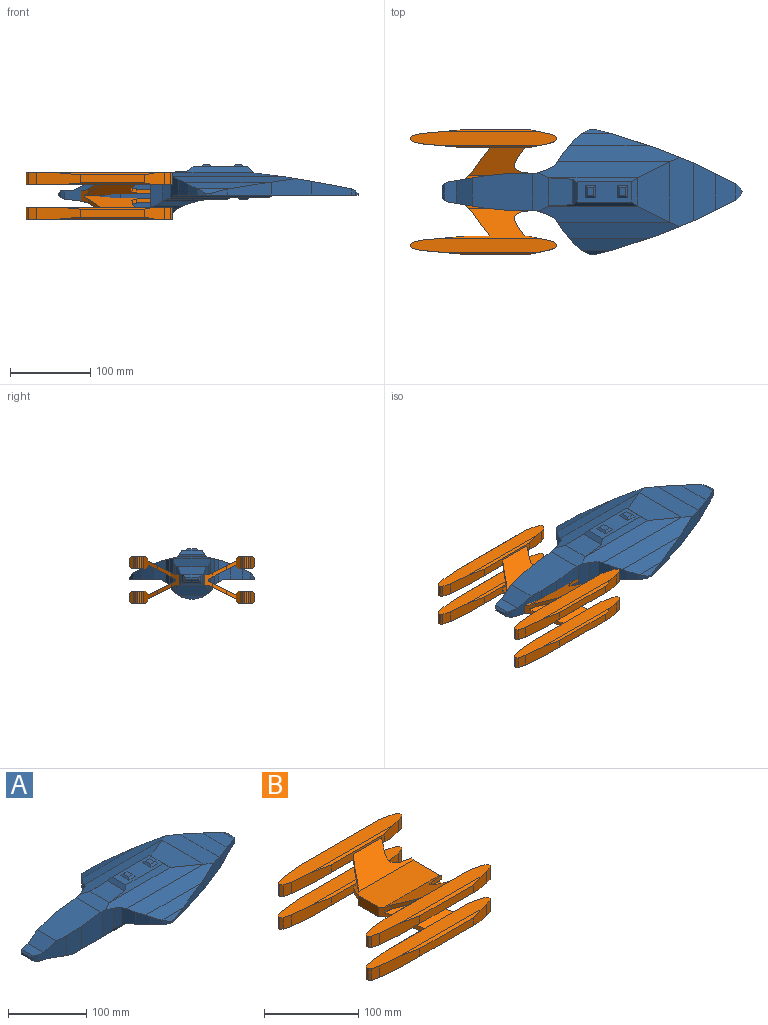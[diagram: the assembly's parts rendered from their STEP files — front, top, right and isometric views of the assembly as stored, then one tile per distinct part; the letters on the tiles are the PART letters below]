
ASSEMBLY  parts=2 mates=3
PART A: 108 faces, bbox 372.5x155x62.5 mm
  f0: plane 7.5x2.5mm, normal (0,-1,0), area 18.8mm2, adj f15,f16,f67,f89
  f1: plane 7.5x2.5mm, normal (0,1,0), area 18.8mm2, adj f27,f28,f67,f84
  f2: plane 10x7.5mm, normal (0,0,1), area 75mm2, adj f53,f68,f78,f91
  f3: plane 10x7.5mm, normal (0,0,1), area 75mm2, adj f69,f77,f79,f90
  f4: plane 67.5x25mm, normal (0,0,1), area 1312.5mm2, adj f52,f53,f68,f69,f75,f77,f78,f79
  f5: plane 7.5x2.5mm, normal (-0.71,-0.71,0), area 17.7mm2, adj f6,f40,f41,f42
  f6: plane 10x5mm, normal (-0.45,-0.89,0), area 48.9mm2, adj f5,f7,f43,f44
  f7: plane 45x31.08mm, normal (-0.16,-0.99,0), area 896.9mm2, adj f6,f8,f44,f45,f46,f47,f48
  f8: plane 36.89x25mm, normal (-0.1,-1,0), area 861.1mm2, adj f7,f9,f46,f47,f103
  f9: plane 40.31x37.5mm, normal (0,-1,0), area 1418.7mm2, adj f8,f10,f47,f50,f103
  f10: plane 40.88x15mm, normal (-0.32,-0.95,0), area 590.7mm2, adj f9,f11,f50,f85,f103,f104
  f11: plane 32.5x10mm, normal (-0.45,-0.89,0), area 331.9mm2, adj f10,f12,f85,f100,f105
  f12: plane 27.5x15mm, normal (-0.83,-0.55,0), area 400mm2, adj f11,f13,f67,f85,f87,f100,f107
  f13: plane 18.75x15mm, normal (-0.77,-0.64,0), area 309.2mm2, adj f12,f14,f67,f87,f88
  f14: plane 12.5x10mm, normal (-0.71,-0.71,0), area 141.4mm2, adj f13,f15,f67,f88
  f15: plane 10x7.5mm, normal (-0.45,-0.89,0), area 55.9mm2, adj f0,f14,f67,f89
  f16: plane 20x7.5mm, normal (0.24,-0.97,0), area 103.1mm2, adj f0,f17,f67,f89
  f17: plane 55x17.5mm, normal (0.3,-0.95,0), area 684.1mm2, adj f16,f18,f67,f87,f88
  f18: plane 50x20.43mm, normal (0.37,-0.93,0), area 991.5mm2, adj f17,f19,f67,f73,f74,f87
  f19: plane 50x25mm, normal (0.45,-0.89,0), area 692.4mm2, adj f18,f20,f67,f72,f74
  f20: plane 7.5x5mm, normal (0.71,-0.71,0), area 44.2mm2, adj f19,f21,f67,f71
  f21: plane 5x5mm, normal (0.89,-0.45,0), area 21mm2, adj f20,f22,f67,f70
  f22: plane 5x5mm, normal (0.89,0.45,0), area 21mm2, adj f21,f23,f67,f70
  f23: plane 7.5x5mm, normal (0.71,0.71,0), area 44.2mm2, adj f22,f24,f67,f71
  f24: plane 50x25mm, normal (0.45,0.89,0), area 692.4mm2, adj f23,f25,f67,f72,f74
  f25: plane 50x20.43mm, normal (0.37,0.93,0), area 991.5mm2, adj f24,f26,f67,f73,f74,f82
  f26: plane 55x17.5mm, normal (0.3,0.95,0), area 684.1mm2, adj f25,f27,f67,f82,f83
  f27: plane 20x7.5mm, normal (0.24,0.97,0), area 103.1mm2, adj f1,f26,f67,f84
  f28: plane 10x7.5mm, normal (-0.45,0.89,0), area 55.9mm2, adj f1,f29,f67,f84
  f29: plane 12.5x10mm, normal (-0.71,0.71,0), area 141.4mm2, adj f28,f30,f67,f83
  f30: plane 18.75x15mm, normal (-0.77,0.64,0), area 309.2mm2, adj f29,f31,f67,f82,f83
  f31: plane 27.5x15mm, normal (-0.83,0.55,0), area 400mm2, adj f30,f32,f67,f80,f82,f92,f94
  f32: plane 32.5x10mm, normal (-0.45,0.89,0), area 331.9mm2, adj f31,f33,f80,f94,f95
  f33: plane 40.88x15mm, normal (-0.32,0.95,0), area 590.7mm2, adj f32,f34,f50,f80,f96,f97
  f34: plane 40.31x37.5mm, normal (0,1,0), area 1418.7mm2, adj f33,f35,f47,f50,f97
  f35: plane 36.89x25mm, normal (-0.1,1,0), area 861.1mm2, adj f34,f36,f46,f47,f97
  f36: plane 45x31.08mm, normal (-0.16,0.99,0), area 896.9mm2, adj f35,f37,f44,f45,f46,f47,f48
  f37: plane 10x5mm, normal (-0.45,0.89,0), area 48.9mm2, adj f36,f38,f43,f44
  f38: plane 7.5x2.5mm, normal (-0.71,0.71,0), area 17.7mm2, adj f37,f40,f41,f42
  f39: plane 15x5mm, normal (0,0,-1), area 75mm2, adj f49,f54,f99,f101
  f40: plane 20x2.5mm, normal (-0.71,0,0.71), area 61.9mm2, adj f5,f38,f41,f44
  f41: plane 15x2.5mm, normal (-1,0,0), area 37.5mm2, adj f5,f38,f40,f42
  f42: plane 20x2.5mm, normal (-0.71,0,-0.71), area 61.9mm2, adj f5,f38,f41,f43
  f43: plane 25x5mm, normal (-0.45,0,-0.89), area 125.8mm2, adj f6,f37,f42,f45
  f44: plane 28.33x15mm, normal (0,0,1), area 379.2mm2, adj f6,f7,f36,f37,f40,f48
  f45: plane 31.67x20mm, normal (-0.12,0,-0.99), area 571.1mm2, adj f7,f36,f43,f46
  f46: plane 47.5x41.88mm, normal (-0.25,0,-0.97), area 1832.8mm2, adj f7,f8,f35,f36,f45,f49,f97,f98
  f47: plane 75x45mm, normal (-0.13,0,0.99), area 3228.3mm2, adj f7,f8,f9,f34,f35,f36,f48,f50
  f48: plane 35x20mm, normal (-0.45,0,0.89), area 708.1mm2, adj f7,f36,f44,f47
  f49: plane 42.5x32.5mm, normal (-0.12,0,-0.99), area 936.1mm2, adj f39,f46,f98,f99,f101,f102
  f50: plane 48x20mm, normal (-0.12,0,0.99), area 868mm2, adj f9,f10,f33,f34,f47,f51,f80,f85
  f51: plane 35x30mm, normal (-0.08,0,1), area 1003.5mm2, adj f50,f52,f81,f86
  f52: plane 31.67x5mm, normal (-0.71,0,0.71), area 200.3mm2, adj f4,f51,f81,f86
  f53: plane 15x2.5mm, normal (-0.71,0,0.71), area 44.2mm2, adj f2,f4,f78,f91
  f54: plane 25x10mm, normal (0.24,0,-0.97), area 154.6mm2, adj f39,f55,f99,f101
  f55: plane 40x5mm, normal (0.71,0,-0.71), area 229.8mm2, adj f54,f56,f98,f102
  f56: plane 50x10mm, normal (0.45,0,-0.89), area 503.1mm2, adj f55,f57,f97,f103
  f57: plane 55x15mm, normal (0.32,0,-0.95), area 830.1mm2, adj f56,f58,f96,f104
  f58: plane 60x15mm, normal (0.16,0,-0.99), area 874.4mm2, adj f57,f59,f95,f105
  f59: plane 60x22.5mm, normal (0,0,-1), area 1350mm2, adj f58,f60,f94,f100
  f60: plane 70x5mm, normal (0.45,0,-0.89), area 363.4mm2, adj f59,f61,f94,f100
  f61: plane 70x7.5mm, normal (0,0,-1), area 525mm2, adj f60,f62,f92,f107
  f62: plane 70x2.5mm, normal (-0.71,0,-0.71), area 229.8mm2, adj f61,f63,f93,f106
  f63: plane 60x10mm, normal (0,0,-1), area 600mm2, adj f62,f64,f93,f106
  f64: plane 70x2.5mm, normal (0.71,0,-0.71), area 229.8mm2, adj f63,f65,f93,f106
  f65: plane 70x25mm, normal (0,0,-1), area 1750mm2, adj f64,f66,f92,f107
  f66: plane 75x5mm, normal (0.45,0,-0.89), area 405.3mm2, adj f65,f67,f92,f107
  f67: plane 229.17x155mm, normal (0,0,-1), area 13491.7mm2, adj f0,f1,f12,f13,f14,f15,f16,f17
  f68: plane 15x2.5mm, normal (0.71,0,0.71), area 44.2mm2, adj f2,f4,f78,f91
  f69: plane 15x2.5mm, normal (-0.71,0,0.71), area 44.2mm2, adj f3,f4,f79,f90
  f70: plane 10x2.5mm, normal (0.71,0,0.71), area 17.7mm2, adj f21,f22,f71
  f71: plane 20x5mm, normal (0.45,0,0.89), area 83.9mm2, adj f20,f23,f70,f72
  f72: plane 45x25mm, normal (0.2,0,0.98), area 828.6mm2, adj f19,f24,f71,f74
  f73: plane 86.05x30mm, normal (0.16,0,0.99), area 2422.4mm2, adj f18,f25,f74,f76,f82,f87
  f74: plane 72x27.5mm, normal (0.18,0,0.98), area 1641.5mm2, adj f18,f19,f24,f25,f72,f73
  f75: plane 35x7.5mm, normal (0.71,0,0.71), area 318.2mm2, adj f4,f76,f81,f86
  f76: plane 75x40mm, normal (0.12,0,0.99), area 2217.1mm2, adj f73,f75,f80,f85
  f77: plane 15x2.5mm, normal (0.71,0,0.71), area 44.2mm2, adj f3,f4,f79,f90
  f78: plane 12.5x2.5mm, normal (0,0.71,0.71), area 35.4mm2, adj f2,f4,f53,f68
  f79: plane 12.5x2.5mm, normal (0,0.71,0.71), area 35.4mm2, adj f3,f4,f69,f77
  f80: plane 163x20mm, normal (0,0.24,0.97), area 2691.4mm2, adj f31,f32,f33,f50,f76,f81,f82
  f81: plane 110x7.5mm, normal (0,0.83,0.55), area 717.4mm2, adj f4,f51,f52,f75,f80
  f82: plane 151.6x20mm, normal (0,0.35,0.94), area 2768.4mm2, adj f25,f26,f30,f31,f73,f80,f83
  f83: plane 98.81x15mm, normal (0,0.45,0.89), area 1147.6mm2, adj f26,f29,f30,f82,f84
  f84: plane 37.5x5mm, normal (0,0.71,0.71), area 159.1mm2, adj f1,f27,f28,f83
  f85: plane 163x20mm, normal (0,-0.24,0.97), area 2691.4mm2, adj f10,f11,f12,f50,f76,f86,f87
  f86: plane 110x7.5mm, normal (0,-0.83,0.55), area 717.4mm2, adj f4,f51,f52,f75,f85
  f87: plane 151.6x20mm, normal (0,-0.35,0.94), area 2768.4mm2, adj f12,f13,f17,f18,f73,f85,f88
  f88: plane 98.81x15mm, normal (0,-0.45,0.89), area 1147.6mm2, adj f13,f14,f17,f87,f89
  f89: plane 37.5x5mm, normal (0,-0.71,0.71), area 159.1mm2, adj f0,f15,f16,f88
  f90: plane 12.5x2.5mm, normal (0,-0.71,0.71), area 35.4mm2, adj f3,f4,f69,f77
  f91: plane 12.5x2.5mm, normal (0,-0.71,0.71), area 35.4mm2, adj f2,f4,f53,f68
  f92: plane 125.83x2.5mm, normal (0,0.71,-0.71), area 433.1mm2, adj f31,f61,f65,f66,f67,f93,f94
  f93: plane 15x5mm, normal (0,0.45,-0.89), area 69.9mm2, adj f62,f63,f64,f92
  f94: plane 80x5mm, normal (0,0.45,-0.89), area 409.9mm2, adj f31,f32,f59,f60,f92,f95
  f95: plane 57.5x2.5mm, normal (0,0.71,-0.71), area 167.9mm2, adj f32,f58,f94,f96
  f96: plane 50x5mm, normal (0,0.89,-0.45), area 216.6mm2, adj f33,f57,f95,f97
  f97: plane 95.58x5mm, normal (0,0.71,-0.71), area 420mm2, adj f33,f34,f35,f46,f56,f96,f98
  f98: plane 82x7.5mm, normal (0,0.55,-0.83), area 604.5mm2, adj f46,f49,f55,f97,f99
  f99: plane 46.25x10mm, normal (0,0.24,-0.97), area 315.7mm2, adj f39,f49,f54,f98
  f100: plane 80x5mm, normal (0,-0.45,-0.89), area 409.9mm2, adj f11,f12,f59,f60,f105,f107
  f101: plane 46.25x10mm, normal (0,-0.24,-0.97), area 315.7mm2, adj f39,f49,f54,f102
  f102: plane 82x7.5mm, normal (0,-0.55,-0.83), area 604.5mm2, adj f46,f49,f55,f101,f103
  f103: plane 95.58x5mm, normal (0,-0.71,-0.71), area 420mm2, adj f8,f9,f10,f46,f56,f102,f104
  f104: plane 50x5mm, normal (0,-0.89,-0.45), area 216.6mm2, adj f10,f57,f103,f105
  f105: plane 57.5x2.5mm, normal (0,-0.71,-0.71), area 167.9mm2, adj f11,f58,f100,f104
  f106: plane 15x5mm, normal (0,-0.45,-0.89), area 69.9mm2, adj f62,f63,f64,f107
  f107: plane 125.83x2.5mm, normal (0,-0.71,-0.71), area 433.1mm2, adj f12,f61,f65,f66,f67,f100,f106
PART B: 136 faces, bbox 182.5x155x57.5 mm
  f0: plane 80x10mm, normal (0,1,0), area 587.5mm2, adj f61,f62,f75,f76,f120,f122,f126,f128
  f1: plane 15x2.5mm, normal (-1,0,0), area 37.5mm2, adj f53,f64,f66,f125
  f2: plane 80x10mm, normal (0,1,0), area 587.5mm2, adj f10,f11,f25,f26,f104,f106,f130,f131
  f3: plane 80x10mm, normal (0,-1,0), area 587.5mm2, adj f37,f38,f50,f51,f109,f113,f118,f121
  f4: plane 80x10mm, normal (0,1,0), area 800mm2, adj f44,f45,f111,f124
  f5: plane 80x10mm, normal (0,1,0), area 800mm2, adj f95,f96,f117,f123
  f6: plane 15x2.5mm, normal (-1,0,0), area 37.5mm2, adj f55,f98,f99,f115
  f7: plane 15x2.5mm, normal (-1,0,0), area 37.5mm2, adj f47,f48,f54,f110
  f8: plane 80x10mm, normal (0,-1,0), area 587.5mm2, adj f88,f89,f101,f102,f105,f107,f112,f116
  f9: plane 17.5x13.75mm, normal (-0.81,-0.58,0), area 107.5mm2, adj f10,f59,f106,f130
  f10: plane 12.5x11.25mm, normal (-0.78,-0.62,0), area 80mm2, adj f2,f9,f106,f130
  f11: plane 55x15mm, normal (-0.09,1,0), area 759.4mm2, adj f2,f12,f56,f104,f131,f132
  f12: plane 15x10mm, normal (-0.24,0.97,0), area 154.6mm2, adj f11,f13,f56,f132
  f13: plane 15x2.5mm, normal (-0.71,0.71,0), area 53mm2, adj f12,f56,f65,f132
  f14: plane 15x2.5mm, normal (-0.71,-0.71,0), area 53mm2, adj f15,f56,f65,f132
  f15: plane 15x10mm, normal (-0.24,-0.97,0), area 154.6mm2, adj f14,f16,f56,f132
  f16: plane 55x15mm, normal (-0.09,-1,0), area 759.4mm2, adj f15,f18,f56,f132,f133,f134
  f17: plane 80x10mm, normal (0,-1,0), area 800mm2, adj f68,f69,f127,f135
  f18: plane 80x10mm, normal (0,-1,0), area 800mm2, adj f16,f19,f133,f134
  f19: plane 25x15mm, normal (0.2,-0.98,0), area 350.6mm2, adj f18,f20,f56,f132,f133,f134
  f20: plane 15x7.5mm, normal (0.32,-0.95,0), area 118.6mm2, adj f19,f21,f56,f132
  f21: plane 15x2.5mm, normal (0.71,-0.71,0), area 53mm2, adj f20,f22,f56,f132
  f22: plane 15x2.5mm, normal (1,0,0), area 37.5mm2, adj f21,f23,f56,f132
  f23: plane 15x2.5mm, normal (0.71,0.71,0), area 53mm2, adj f22,f24,f56,f132
  f24: plane 15x7.5mm, normal (0.32,0.95,0), area 118.6mm2, adj f23,f25,f56,f132
  f25: plane 25x15mm, normal (0.2,0.98,0), area 350.6mm2, adj f2,f24,f56,f104,f131,f132
  f26: plane 15x12.5mm, normal (0.83,0.55,0), area 90.1mm2, adj f2,f27,f106,f130
  f27: plane 7.5x5mm, normal (0.89,0.45,0), area 28mm2, adj f26,f28,f106,f130
  f28: plane 7.5x5mm, normal (1,0,0), area 25mm2, adj f27,f29,f106,f130
  f29: plane 6.25x2.5mm, normal (0.71,-0.71,0), area 17.7mm2, adj f28,f30,f106,f130
  f30: plane 6.25x5mm, normal (0.45,-0.89,0), area 28mm2, adj f29,f31,f106,f130
  f31: plane 17.5x6.25mm, normal (0.14,-0.99,0), area 88.4mm2, adj f30,f82,f106,f130
  f32: plane 17.5x6.25mm, normal (0.14,0.99,0), area 88.4mm2, adj f33,f82,f113,f118
  f33: plane 6.25x5mm, normal (0.45,0.89,0), area 28mm2, adj f32,f34,f113,f118
  f34: plane 6.25x2.5mm, normal (0.71,0.71,0), area 17.7mm2, adj f33,f35,f113,f118
  f35: plane 7.5x5mm, normal (1,0,0), area 25mm2, adj f34,f36,f113,f118
  f36: plane 7.5x5mm, normal (0.89,-0.45,0), area 28mm2, adj f35,f37,f113,f118
  f37: plane 15x12.5mm, normal (0.83,-0.55,0), area 90.1mm2, adj f3,f36,f113,f118
  f38: plane 25x15mm, normal (0.2,-0.98,0), area 350.6mm2, adj f3,f39,f54,f109,f110,f121
  f39: plane 15x7.5mm, normal (0.32,-0.95,0), area 118.6mm2, adj f38,f40,f54,f110
  f40: plane 15x2.5mm, normal (0.71,-0.71,0), area 53mm2, adj f39,f41,f54,f110
  f41: plane 15x2.5mm, normal (1,0,0), area 37.5mm2, adj f40,f42,f54,f110
  f42: plane 15x2.5mm, normal (0.71,0.71,0), area 53mm2, adj f41,f43,f54,f110
  f43: plane 15x7.5mm, normal (0.32,0.95,0), area 118.6mm2, adj f42,f44,f54,f110
  f44: plane 25x15mm, normal (0.2,0.98,0), area 350.6mm2, adj f4,f43,f54,f110,f111,f124
  f45: plane 55x15mm, normal (-0.09,1,0), area 759.4mm2, adj f4,f46,f54,f110,f111,f124
  f46: plane 15x10mm, normal (-0.24,0.97,0), area 154.6mm2, adj f45,f47,f54,f110
  f47: plane 15x2.5mm, normal (-0.71,0.71,0), area 53mm2, adj f7,f46,f54,f110
  f48: plane 15x2.5mm, normal (-0.71,-0.71,0), area 53mm2, adj f7,f49,f54,f110
  f49: plane 15x10mm, normal (-0.24,-0.97,0), area 154.6mm2, adj f48,f50,f54,f110
  f50: plane 55x15mm, normal (-0.09,-1,0), area 759.4mm2, adj f3,f49,f54,f109,f110,f121
  f51: plane 12.5x11.25mm, normal (-0.78,0.62,0), area 80mm2, adj f3,f52,f113,f118
  f52: plane 17.5x13.75mm, normal (-0.81,0.58,0), area 107.5mm2, adj f51,f57,f113,f118
  f53: plane 182.5x17.5mm, normal (0,0,1), area 2900mm2, adj f1,f62,f63,f64,f66,f67,f68,f69
  f54: plane 182.5x17.5mm, normal (0,0,1), area 2900mm2, adj f7,f38,f39,f40,f41,f42,f43,f44
  f55: plane 182.5x17.5mm, normal (0,0,-1), area 2900mm2, adj f6,f89,f90,f91,f92,f93,f94,f95
  f56: plane 182.5x17.5mm, normal (0,0,-1), area 2900mm2, adj f11,f12,f13,f14,f15,f16,f19,f20
  f57: plane 17.5x10mm, normal (-0.71,0.71,0), area 159.1mm2, adj f52,f58,f103,f107,f108,f112,f113,f114
  f58: plane 30x12.5mm, normal (-1,0,0), area 375mm2, adj f57,f59,f108,f119
  f59: plane 17.5x10mm, normal (-0.71,-0.71,0), area 159.1mm2, adj f9,f58,f60,f106,f108,f119,f120,f128
  f60: plane 17.5x13.75mm, normal (-0.81,-0.58,0), area 107.5mm2, adj f59,f61,f120,f128
  f61: plane 12.5x11.25mm, normal (-0.78,-0.62,0), area 80mm2, adj f0,f60,f120,f128
  f62: plane 55x15mm, normal (-0.09,1,0), area 759.4mm2, adj f0,f53,f63,f122,f125,f126
  f63: plane 15x10mm, normal (-0.24,0.97,0), area 154.6mm2, adj f53,f62,f64,f125
  f64: plane 15x2.5mm, normal (-0.71,0.71,0), area 53mm2, adj f1,f53,f63,f125
  f65: plane 15x2.5mm, normal (-1,0,0), area 37.5mm2, adj f13,f14,f56,f132
  f66: plane 15x2.5mm, normal (-0.71,-0.71,0), area 53mm2, adj f1,f53,f67,f125
  f67: plane 15x10mm, normal (-0.24,-0.97,0), area 154.6mm2, adj f53,f66,f68,f125
  f68: plane 55x15mm, normal (-0.09,-1,0), area 759.4mm2, adj f17,f53,f67,f125,f127,f135
  f69: plane 25x15mm, normal (0.2,-0.98,0), area 350.6mm2, adj f17,f53,f70,f125,f127,f135
  f70: plane 15x7.5mm, normal (0.32,-0.95,0), area 118.6mm2, adj f53,f69,f71,f125
  f71: plane 15x2.5mm, normal (0.71,-0.71,0), area 53mm2, adj f53,f70,f72,f125
  f72: plane 15x2.5mm, normal (1,0,0), area 37.5mm2, adj f53,f71,f73,f125
  f73: plane 15x2.5mm, normal (0.71,0.71,0), area 53mm2, adj f53,f72,f74,f125
  f74: plane 15x7.5mm, normal (0.32,0.95,0), area 118.6mm2, adj f53,f73,f75,f125
  f75: plane 25x15mm, normal (0.2,0.98,0), area 350.6mm2, adj f0,f53,f74,f122,f125,f126
  f76: plane 15x12.5mm, normal (0.83,0.55,0), area 90.1mm2, adj f0,f77,f120,f128
  f77: plane 7.5x5mm, normal (0.89,0.45,0), area 28mm2, adj f76,f78,f120,f128
  f78: plane 7.5x5mm, normal (1,0,0), area 25mm2, adj f77,f79,f120,f128
  f79: plane 6.25x2.5mm, normal (0.71,-0.71,0), area 17.7mm2, adj f78,f80,f120,f128
  f80: plane 6.25x5mm, normal (0.45,-0.89,0), area 28mm2, adj f79,f81,f120,f128
  f81: plane 17.5x6.25mm, normal (0.14,-0.99,0), area 88.4mm2, adj f80,f82,f120,f128
  f82: plane 45x15mm, normal (1,0,0), area 550mm2, adj f31,f32,f81,f83,f106,f107,f108,f112
  f83: plane 17.5x6.25mm, normal (0.14,0.99,0), area 88.4mm2, adj f82,f84,f107,f112
  f84: plane 6.25x5mm, normal (0.45,0.89,0), area 28mm2, adj f83,f85,f107,f112
  f85: plane 6.25x2.5mm, normal (0.71,0.71,0), area 17.7mm2, adj f84,f86,f107,f112
  f86: plane 7.5x5mm, normal (1,0,0), area 25mm2, adj f85,f87,f107,f112
  f87: plane 7.5x5mm, normal (0.89,-0.45,0), area 28mm2, adj f86,f88,f107,f112
  f88: plane 15x12.5mm, normal (0.83,-0.55,0), area 90.1mm2, adj f8,f87,f107,f112
  f89: plane 25x15mm, normal (0.2,-0.98,0), area 350.6mm2, adj f8,f55,f90,f105,f115,f116
  f90: plane 15x7.5mm, normal (0.32,-0.95,0), area 118.6mm2, adj f55,f89,f91,f115
  f91: plane 15x2.5mm, normal (0.71,-0.71,0), area 53mm2, adj f55,f90,f92,f115
  f92: plane 15x2.5mm, normal (1,0,0), area 37.5mm2, adj f55,f91,f93,f115
  f93: plane 15x2.5mm, normal (0.71,0.71,0), area 53mm2, adj f55,f92,f94,f115
  f94: plane 15x7.5mm, normal (0.32,0.95,0), area 118.6mm2, adj f55,f93,f95,f115
  f95: plane 25x15mm, normal (0.2,0.98,0), area 350.6mm2, adj f5,f55,f94,f115,f117,f123
  f96: plane 55x15mm, normal (-0.09,1,0), area 759.4mm2, adj f5,f55,f97,f115,f117,f123
  f97: plane 15x10mm, normal (-0.24,0.97,0), area 154.6mm2, adj f55,f96,f98,f115
  f98: plane 15x2.5mm, normal (-0.71,0.71,0), area 53mm2, adj f6,f55,f97,f115
  f99: plane 15x2.5mm, normal (-0.71,-0.71,0), area 53mm2, adj f6,f55,f100,f115
  f100: plane 15x10mm, normal (-0.24,-0.97,0), area 154.6mm2, adj f55,f99,f101,f115
  f101: plane 55x15mm, normal (-0.09,-1,0), area 759.4mm2, adj f8,f55,f100,f105,f115,f116
  f102: plane 12.5x11.25mm, normal (-0.78,0.62,0), area 80mm2, adj f8,f103,f107,f112
  f103: plane 17.5x13.75mm, normal (-0.81,0.58,0), area 107.5mm2, adj f57,f102,f107,f112
  f104: plane 120x2.5mm, normal (0,0.71,-0.71), area 353.6mm2, adj f2,f11,f25,f56
  f105: plane 120x2.5mm, normal (0,-0.71,-0.71), area 353.6mm2, adj f8,f55,f89,f101
  f106: plane 82.5x35mm, normal (0,0.45,-0.89), area 1967mm2, adj f2,f9,f10,f26,f27,f28,f29,f30
  f107: plane 82.5x35mm, normal (0,-0.45,-0.89), area 1967mm2, adj f8,f57,f82,f83,f84,f85,f86,f87
  f108: plane 87.5x40mm, normal (0,0,-1), area 3475mm2, adj f57,f58,f59,f82,f106,f107
  f109: plane 120x2.5mm, normal (0,-0.71,-0.71), area 353.6mm2, adj f3,f38,f50,f110
  f110: plane 182.5x17.5mm, normal (0,0,-1), area 2900mm2, adj f7,f38,f39,f40,f41,f42,f43,f44
  f111: plane 120x2.5mm, normal (0,0.71,-0.71), area 353.6mm2, adj f4,f44,f45,f110
  f112: plane 82.5x35mm, normal (0,0.45,0.89), area 1967mm2, adj f8,f57,f82,f83,f84,f85,f86,f87
  f113: plane 82.5x35mm, normal (0,0.45,-0.89), area 1967mm2, adj f3,f32,f33,f34,f35,f36,f37,f51
  f114: plane 82.5x2.5mm, normal (0,1,0), area 206.2mm2, adj f57,f82,f112,f113
  f115: plane 182.5x17.5mm, normal (0,0,1), area 2900mm2, adj f6,f89,f90,f91,f92,f93,f94,f95
  f116: plane 120x2.5mm, normal (0,-0.71,0.71), area 353.6mm2, adj f8,f89,f101,f115
  f117: plane 120x2.5mm, normal (0,0.71,0.71), area 353.6mm2, adj f5,f95,f96,f115
  f118: plane 82.5x35mm, normal (0,-0.45,0.89), area 1967mm2, adj f3,f32,f33,f34,f35,f36,f37,f51
  f119: plane 87.5x40mm, normal (0,0,1), area 3475mm2, adj f57,f58,f59,f82,f118,f120
  f120: plane 82.5x35mm, normal (0,0.45,0.89), area 1967mm2, adj f0,f59,f60,f61,f76,f77,f78,f79
  f121: plane 120x2.5mm, normal (0,-0.71,0.71), area 353.6mm2, adj f3,f38,f50,f54
  f122: plane 120x2.5mm, normal (0,0.71,0.71), area 353.6mm2, adj f0,f53,f62,f75
  f123: plane 120x2.5mm, normal (0,0.71,-0.71), area 353.6mm2, adj f5,f55,f95,f96
  f124: plane 120x2.5mm, normal (0,0.71,0.71), area 353.6mm2, adj f4,f44,f45,f54
  f125: plane 182.5x17.5mm, normal (0,0,-1), area 2900mm2, adj f1,f62,f63,f64,f66,f67,f68,f69
  f126: plane 120x2.5mm, normal (0,0.71,-0.71), area 353.6mm2, adj f0,f62,f75,f125
  f127: plane 120x2.5mm, normal (0,-0.71,-0.71), area 353.6mm2, adj f17,f68,f69,f125
  f128: plane 82.5x35mm, normal (0,-0.45,-0.89), area 1967mm2, adj f0,f59,f60,f61,f76,f77,f78,f79
  f129: plane 82.5x2.5mm, normal (0,-1,0), area 206.2mm2, adj f59,f82,f128,f130
  f130: plane 82.5x35mm, normal (0,-0.45,0.89), area 1967mm2, adj f2,f9,f10,f26,f27,f28,f29,f30
  f131: plane 120x2.5mm, normal (0,0.71,0.71), area 353.6mm2, adj f2,f11,f25,f132
  f132: plane 182.5x17.5mm, normal (0,0,1), area 2900mm2, adj f11,f12,f13,f14,f15,f16,f19,f20
  f133: plane 120x2.5mm, normal (0,-0.71,0.71), area 353.6mm2, adj f16,f18,f19,f132
  f134: plane 120x2.5mm, normal (0,-0.71,-0.71), area 353.6mm2, adj f16,f18,f19,f56
  f135: plane 120x2.5mm, normal (0,-0.71,0.71), area 353.6mm2, adj f17,f53,f68,f69
PLACE A t=(31.45,68.47,-90.18)mm
PLACE B t=(32.53,68.47,-95.18)mm
MATE parallel B.f58 <-> A.f41  axis (-1,0,0) through (100.03,148.47,-91.43)mm
MATE planar B.f119 <-> A.f44  axis (0,0,1) through (144.08,148.47,-85.18)mm
MATE fastened B.f119 <-> A.f44  axis (0,0,1) through (100.03,148.47,-85.18)mm
